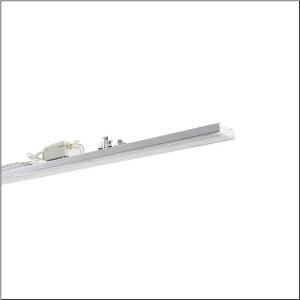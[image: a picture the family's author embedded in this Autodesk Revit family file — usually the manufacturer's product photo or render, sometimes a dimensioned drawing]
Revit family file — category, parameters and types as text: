
# Revit family: licross_r__21_recessed_mo_52tl11dn47xg_06fb
name_source: partatom
category: Lighting Fixtures
units: mm (PartAtom-declared; Revit-internal decimal feet)

## family parameters
Cut with Voids When Loaded = No
Host = Face
Light Source = No
Part Type = Normal
Room Calculation Point = No
Round Connector Dimension = Use Diameter
Shared = No

## types (1)
- --- (1 x LED, 7120 lm, 39.3 W, 4000K)
    Apparent Load = 39 VA
    CIE Flux Codes = 89 96 99 100 100
    Color Rendering = 80
    Color Temperature = 4000K
    Default Elevation = 1800 mm
    Description = Licross® 21 Recessed MO, luminaire insert, of sheet steel, galvanised, coil coated, white, length: 1.500mm, width: 66mm, height: 67mm, LED rated luminous flux: 7.120lm, light colour: 840, control gear: DALI 2, with plug, 5-pole, with phase selection, mains connection: 220..240V, AC, 50/60Hz, rated input power: 39W, halogen-free wiring, primary light control with lens, of plastic, primary optical cover: cover, of PMMA, light emission: direct distribution, primary light characteristic: symmetric, protection rating (complete): IP40, insulation class (complete): insulation class I (protective earthing), certification: CE, ENEC, VDE, UKCA, protection symbol: D if used in an environment without relevant dust loads with corresponding accessories, impact resistance: IK06, permissible ambient temperature for indoor applications: -25..+40°C, corresponds to IFS (International Featured Standards) requirements for safety and quality in the food industry, reducing of maximum allowable ambient temperature of 5°C with ceiling mounting, LABS conformity tested according to VDMA 24364:2018-05, packaging unit: 1 piece
    Height = 58 mm
    Lamp = 1 x LED
    Lamp Light Flux = 7120 lm
    Lamp Power = 39.3 W
    Lamp count = 1
    Length = 1500 mm
    Luminous efficacy = 181 lm/W
    Manufacturer = Siteco
    ModVariant = No
    Model = 52TL11DN47XG
    Mounting Place = Ceiling
    Mounting Type = Pendant
    Number of Poles = 1
    OnlyDefault = Yes
    Power Factor = 1
    Product Name = Licross® 21 Recessed MO
    Product group = luminaire insert
    ProductGroupID = 901
    Protection Class = Protection class I
    Protection Degree = IP 40
    RLX_Detail_Level = 1
    RLX_Emergency_Light_Flux = 0 lm
    RLX_Emergency_Type = 0
    RLX_Emergency_Type_DB = No
    RlxData = <blob elided: 24077 chars, md5=83153f8b>
    Socket = socket
    Standby Power = 0 W
    System Light Flux = 7120 lm
    System Power = 39 W
    Type Comments = factory setting: luminous flux: 100 % | dim-lin: 254 | 267 mA
    Type Image = l_1296930.jpg
    URL = http://relux.com
    VarID = @adj_058539
    Voltage = 0 V
    Weight = 0.00 kg
    Width = 66 mm

## geometry (parser evidence)
native form markers: Blend x4, Sweep x11
no freeform markers — native parametric forms only
